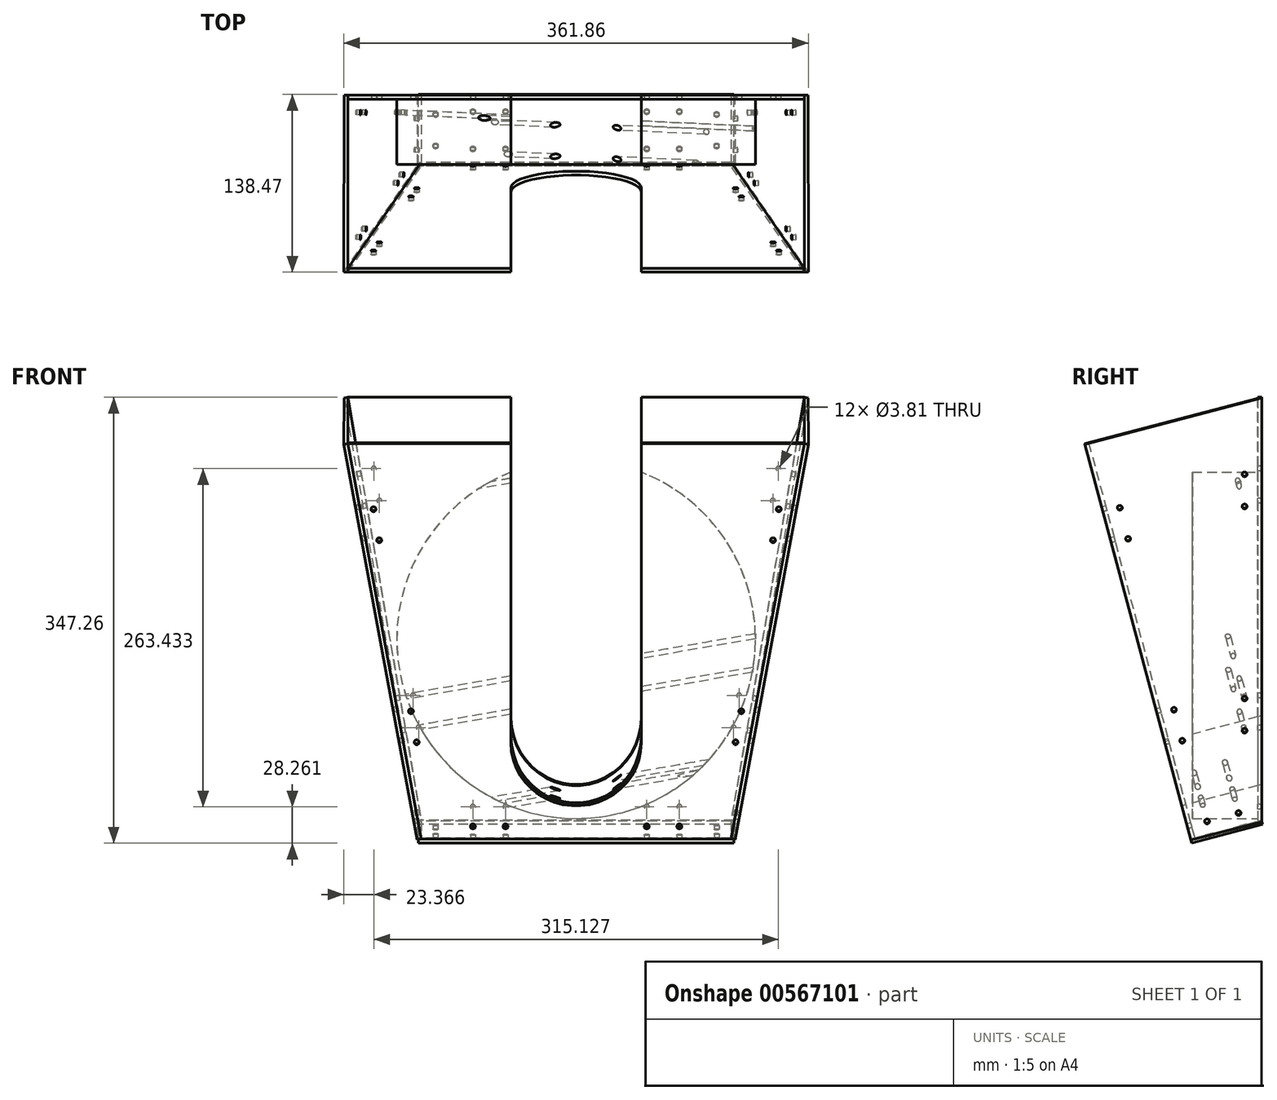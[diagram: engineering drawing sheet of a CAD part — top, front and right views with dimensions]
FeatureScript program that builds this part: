
annotation { "Feature Type Name" : "Feature", "Feature Type Description" : "" }
export const myFeature = defineFeature(function(context is Context, id is Id, definition is map)
    precondition{}
    {
        {
            var Q0;
            Q0=qCreatedBy(makeId("Right.planeOp"),FACE);
            var sketch = newSketch(context, id + "F0", { "sketchPlane" : qUnion([Q0])});
            skLineSegment(sketch, "E0.bottom", {"start": v(-164.52, 79.35) * mm, "end": v(-89.48, 66.12) * mm});
            skLineSegment(sketch, "E0.top", {"start": v(-67.49, 629.66) * mm, "end": v(7.56, 616.43) * mm});
            skLineSegment(sketch, "E0.left", {"start": v(-164.52, 79.35) * mm, "end": v(-67.49, 629.66) * mm});
            skLineSegment(sketch, "E0.right", {"start": v(-89.48, 66.12) * mm, "end": v(7.56, 616.43) * mm});
            skLineSegment(sketch, "E1.bottom", {"start": v(0, 38.1) * mm, "end": v(406.4, 38.1) * mm});
            skLineSegment(sketch, "E1.top", {"start": v(0, 546.1) * mm, "end": v(406.4, 546.1) * mm});
            skLineSegment(sketch, "E1.left", {"start": v(0, 38.1) * mm, "end": v(0, 546.1) * mm});
            skLineSegment(sketch, "E1.right", {"start": v(406.4, 38.1) * mm, "end": v(406.4, 546.1) * mm});
            skLineSegment(sketch, "E2.bottom", {"start": v(42.48, 128.48) * mm, "end": v(86.93, 128.48) * mm});
            skLineSegment(sketch, "E2.top", {"start": v(42.48, 84.03) * mm, "end": v(86.93, 84.03) * mm});
            skLineSegment(sketch, "E2.left", {"start": v(42.48, 128.48) * mm, "end": v(42.48, 84.03) * mm});
            skLineSegment(sketch, "E2.right", {"start": v(86.93, 128.48) * mm, "end": v(86.93, 84.03) * mm});
            skPoint(sketch, "E2.middle", {"position": v(64.7, 106.26) * mm});
            skSolve(sketch);
        }
        {
            var Q0;
            Q0=qCreatedBy(makeId("Front.planeOp"),FACE);
            var sketch = newSketch(context, id + "F1", { "sketchPlane" : qUnion([Q0])});
            skLineSegment(sketch, "E3.bottom", {"start": v(177.8, 596.9) * mm, "end": v(-177.8, 596.9) * mm});
            skLineSegment(sketch, "E3.top", {"start": v(120.65, 266.7) * mm, "end": v(-120.65, 266.7) * mm});
            skPoint(sketch, "E3.middle", {"position": v(0, 431.8) * mm});
            skLineSegment(sketch, "E4", {"start": v(-177.8, 596.9) * mm, "end": v(-120.65, 266.7) * mm});
            skLineSegment(sketch, "E5", {"start": v(0, 596.9) * mm, "end": v(0, 604.14) * mm, "construction": true});
            skPoint(sketch, "E5.endSnap0", {"position": v(0, 596.9) * mm});
            skLineSegment(sketch, "E6.MirrorCS", {"start": v(177.8, 596.9) * mm, "end": v(120.65, 266.7) * mm});
            skCircle(sketch, "E7", {"center": v(0, 408.44) * mm, "radius": 139.7 * mm, "construction": true});
            skCircle(sketch, "E8", {"center": v(0, 330.2) * mm, "radius": 17.46 * mm, "construction": true});
            skPoint(sketch, "E3.left.end.orphan", {"position": v(177.8, 266.7) * mm});
            skPoint(sketch, "E9.orphan", {"position": v(-177.8, 266.7) * mm});
            skSolve(sketch);
        }
        {
            var Q0;
            Q0=qSketchRegion(id+"F1",true);
            extrude(context, id + "F2", {"entities" : qUnion([Q0]), "oppositeDirection" : true, "depth" : 3.17 * mm});
        }
        {
            var Q0;
            Q0=makeQuery(id+"F1.imprint","IMPRINT",FACE,{"disambiguationData":[TD([[makeQuery(id+"F1.imprint","IMPRINT",EDGE,{"derivedFrom":sQuery(id+"F1.wireOp",EDGE,"E3.bottom")}),1.0]])]});
            var sketch = newSketch(context, id + "F3", { "sketchPlane" : qUnion([Q0])});
            skCircle(sketch, "E10.0", {"center": v(0, 408.44) * mm, "radius": 139.7 * mm});
            skSolve(sketch);
        }
        {
            var Q0;
            Q0=qSketchRegion(id+"F3",true);
            extrude(context, id + "F4", {"entities" : qUnion([Q0]), "depth" : 50.8 * mm});
        }
        {
            var Q0;
            Q0=makeQuery(id+"F4.opExtrude","CAP_FACE",FACE,{"disambiguationData":[OSD([sQuery(id+"F3.wireOp",EDGE,"E10.0")])],"isStart":false});
            var Q1;
            Q1=sQuery(id+"F1.wireOp",EDGE,"E3.top");
            cPlane(context, id + "F5", {"entities" : qUnion([Q0, Q1]), "cplaneType" : CPlaneType.LINE_ANGLE, "offset" : 25.4 * mm, "angle" : 345 * degree, "width" : 152.4 * mm, "height" : 152.4 * mm});
        }
        {
            var Q0;
            Q0=qCreatedBy(id+"F5.planeOp",FACE);
            cPlane(context, id + "F6", {"entities" : qUnion([Q0]), "cplaneType" : CPlaneType.OFFSET, "offset" : 53.97 * mm, "oppositeDirection" : true, "width" : 152.4 * mm, "height" : 152.4 * mm});
        }
        {
            var Q0;
            Q0=qCreatedBy(id+"F6.planeOp",FACE);
            var sketch = newSketch(context, id + "F7", { "sketchPlane" : qUnion([Q0])});
            skLineSegment(sketch, "E11.0", {"start": v(177.8, 576.56) * mm, "end": v(120.65, 257.61) * mm});
            skLineSegment(sketch, "E11.1", {"start": v(-177.8, 576.56) * mm, "end": v(177.8, 576.56) * mm});
            skLineSegment(sketch, "E11.2", {"start": v(-177.8, 576.56) * mm, "end": v(-120.65, 257.61) * mm});
            skLineSegment(sketch, "E11.3", {"start": v(-120.65, 257.61) * mm, "end": v(120.65, 257.61) * mm});
            skSolve(sketch);
        }
        {
            var Q0;
            Q0=makeQuery(id+"F7.imprint","IMPRINT",FACE,{"disambiguationData":[TD([[makeQuery(id+"F7.imprint","IMPRINT",EDGE,{"derivedFrom":sQuery(id+"F7.wireOp",EDGE,"E11.0")}),-1.0]])]});
            extrude(context, id + "F8", {"entities" : qUnion([Q0]), "depth" : 3.17 * mm});
        }
        {
            var Q0;
            Q0=makeQuery(id+"F8.opExtrude","SWEPT_FACE",FACE,{"disambiguationData":[OSD([sQuery(id+"F7.wireOp",EDGE,"E11.0")])]});
            var sketch = newSketch(context, id + "F9", { "sketchPlane" : qUnion([Q0])});
            skLineSegment(sketch, "E12.0", {"start": v(0.18, 618.48) * mm, "end": v(0.18, 283.37) * mm});
            skLineSegment(sketch, "E13.0", {"start": v(138.18, 582.92) * mm, "end": v(55.54, 269.6) * mm});
            skLineSegment(sketch, "E14", {"start": v(0.18, 283.37) * mm, "end": v(52.47, 270.41) * mm});
            skLineSegment(sketch, "E15", {"start": v(0.18, 618.48) * mm, "end": v(138.18, 582.92) * mm});
            skSolve(sketch);
        }
        {
            var Q0;
            {var subQ0=sQuery(id+"F9.wireOp",EDGE,"E12.0");Q0=makeQuery(id+"F9.imprint","IMPRINT",FACE,{"disambiguationData":[TD([[makeQuery(id+"F9.imprint","IMPRINT",EDGE,{"derivedFrom":subQ0}),1.0]])]});}
            var Q1;
            {var subQ0=sQuery(id+"F9.wireOp",EDGE,"E13.0");Q1=makeQuery(id+"F9.imprint","IMPRINT",FACE,{"disambiguationData":[TD([[makeQuery(id+"F9.imprint","IMPRINT",EDGE,{"derivedFrom":subQ0}),-1.0]])]});}
            extrude(context, id + "F10", {"entities" : qUnion([Q0, Q1]), "depth" : 3.17 * mm});
        }
        {
            var Q0;
            Q0=makeQuery(id+"F10.opExtrude","SWEPT_BODY",BODY,{"disambiguationData":[OSD([sQuery(id+"F7.wireOp",EDGE,"E11.0"),sQuery(id+"F9.wireOp",EDGE,"E12.0"),sQuery(id+"F9.wireOp",EDGE,"E14"),sQuery(id+"F9.wireOp",EDGE,"E15")])]});
            var Q1;
            Q1=qCreatedBy(makeId("Right.planeOp"),FACE);
            mirror(context, id + "F11", {"entities" : qUnion([Q0]), "mirrorPlane" : qUnion([Q1])});
        }
        {
            var Q0;
            Q0=makeQuery(id+"F8.opExtrude","SWEPT_FACE",FACE,{"disambiguationData":[OSD([sQuery(id+"F7.wireOp",EDGE,"E11.3")])]});
            var sketch = newSketch(context, id + "F12", { "sketchPlane" : qUnion([Q0])});
            skLineSegment(sketch, "E16.bottom", {"start": v(122.9, -15.05) * mm, "end": v(-122.9, -15.05) * mm});
            skLineSegment(sketch, "E16.top", {"start": v(122.9, -72.1) * mm, "end": v(-122.9, -72.1) * mm});
            skLineSegment(sketch, "E16.left", {"start": v(122.9, -15.05) * mm, "end": v(122.9, -72.1) * mm});
            skLineSegment(sketch, "E16.right", {"start": v(-122.9, -15.05) * mm, "end": v(-122.9, -72.1) * mm});
            skPoint(sketch, "E16.middle", {"position": v(0, -43.57) * mm});
            skSolve(sketch);
        }
        {
            var Q0;
            Q0=qSketchRegion(id+"F12",true);
            extrude(context, id + "F13", {"entities" : qUnion([Q0]), "depth" : 3.17 * mm});
        }
        {
            var Q0;
            Q0=makeQuery(id+"F8.opExtrude","CAP_FACE",FACE,{"disambiguationData":[OSD([sQuery(id+"F7.wireOp",EDGE,"E11.0"),sQuery(id+"F7.wireOp",EDGE,"E11.1"),sQuery(id+"F7.wireOp",EDGE,"E11.2"),sQuery(id+"F7.wireOp",EDGE,"E11.3")])],"isStart":true});
            var sketch = newSketch(context, id + "F14", { "sketchPlane" : qUnion([Q0])});
            skLineSegment(sketch, "E17", {"start": v(0, 439.09) * mm, "end": v(0, 333.36) * mm, "construction": true});
            skLineSegment(sketch, "E18.bottom", {"start": v(-170.23, 534.32) * mm, "end": v(-149.92, 537.96) * mm, "construction": true});
            skLineSegment(sketch, "E18.top", {"start": v(-161.27, 484.32) * mm, "end": v(-140.96, 487.96) * mm, "construction": true});
            skLineSegment(sketch, "E18.left", {"start": v(-170.23, 534.32) * mm, "end": v(-161.27, 484.32) * mm, "construction": true});
            skLineSegment(sketch, "E18.right", {"start": v(-149.92, 537.96) * mm, "end": v(-140.96, 487.96) * mm, "construction": true});
            skLineSegment(sketch, "E19.bottom", {"start": v(-93.12, 278.25) * mm, "end": v(-42.32, 278.25) * mm, "construction": true});
            skLineSegment(sketch, "E19.top", {"start": v(-93.12, 257.61) * mm, "end": v(-42.32, 257.61) * mm});
            skLineSegment(sketch, "E19.left", {"start": v(-93.12, 278.25) * mm, "end": v(-93.12, 257.61) * mm, "construction": true});
            skLineSegment(sketch, "E19.right", {"start": v(-42.32, 278.25) * mm, "end": v(-42.32, 257.61) * mm, "construction": true});
            skLineSegment(sketch, "E20", {"start": v(-160.07, 536.14) * mm, "end": v(-151.11, 486.14) * mm, "construction": true});
            skLineSegment(sketch, "E21", {"start": v(-93.12, 267.93) * mm, "end": v(-42.32, 267.93) * mm, "construction": true});
            skLineSegment(sketch, "E22", {"start": v(-145.44, 512.96) * mm, "end": v(-165.75, 509.32) * mm, "construction": true});
            skLineSegment(sketch, "E23", {"start": v(-67.72, 278.25) * mm, "end": v(-67.72, 257.61) * mm, "construction": true});
            skCircle(sketch, "E24", {"center": v(-157.83, 523.64) * mm, "radius": 1.9 * mm});
            skCircle(sketch, "E25.MirrorC", {"center": v(-153.35, 498.64) * mm, "radius": 1.9 * mm});
            skLineSegment(sketch, "E26.bottom", {"start": v(-141.04, 371.42) * mm, "end": v(-120.73, 375.06) * mm, "construction": true});
            skLineSegment(sketch, "E26.top", {"start": v(-132.08, 321.41) * mm, "end": v(-111.77, 325.05) * mm, "construction": true});
            skLineSegment(sketch, "E26.left", {"start": v(-141.04, 371.42) * mm, "end": v(-132.08, 321.41) * mm, "construction": true});
            skLineSegment(sketch, "E26.right", {"start": v(-120.73, 375.06) * mm, "end": v(-111.77, 325.05) * mm, "construction": true});
            skLineSegment(sketch, "E27", {"start": v(-130.88, 373.24) * mm, "end": v(-121.92, 323.23) * mm, "construction": true});
            skLineSegment(sketch, "E28", {"start": v(-116.25, 350.05) * mm, "end": v(-136.56, 346.41) * mm, "construction": true});
            skCircle(sketch, "E29", {"center": v(-128.64, 360.73) * mm, "radius": 1.9 * mm});
            skCircle(sketch, "E30.MirrorC", {"center": v(-124.16, 335.73) * mm, "radius": 1.9 * mm});
            skCircle(sketch, "E31", {"center": v(-80.42, 267.93) * mm, "radius": 1.9 * mm});
            skCircle(sketch, "E32.MirrorC", {"center": v(-55.02, 267.93) * mm, "radius": 1.9 * mm});
            skLineSegment(sketch, "E33.MirrorCS", {"start": v(132.08, 321.41) * mm, "end": v(111.77, 325.05) * mm, "construction": true});
            skCircle(sketch, "E34.MirrorC", {"center": v(128.64, 360.73) * mm, "radius": 1.9 * mm});
            skCircle(sketch, "E35.MirrorC", {"center": v(157.83, 523.64) * mm, "radius": 1.9 * mm});
            skLineSegment(sketch, "E36.MirrorCS", {"start": v(42.32, 278.25) * mm, "end": v(42.32, 257.61) * mm, "construction": true});
            skLineSegment(sketch, "E37.MirrorCS", {"start": v(93.12, 278.25) * mm, "end": v(93.12, 257.61) * mm, "construction": true});
            skLineSegment(sketch, "E38.MirrorCS", {"start": v(161.27, 484.32) * mm, "end": v(140.96, 487.96) * mm, "construction": true});
            skCircle(sketch, "E39.MirrorC", {"center": v(55.02, 267.93) * mm, "radius": 1.9 * mm});
            skLineSegment(sketch, "E40.MirrorCS", {"start": v(145.44, 512.96) * mm, "end": v(165.75, 509.32) * mm, "construction": true});
            skLineSegment(sketch, "E41.MirrorCS", {"start": v(170.23, 534.32) * mm, "end": v(149.92, 537.96) * mm, "construction": true});
            skLineSegment(sketch, "E42.MirrorCS", {"start": v(130.88, 373.24) * mm, "end": v(121.92, 323.23) * mm, "construction": true});
            skCircle(sketch, "E43.MirrorC", {"center": v(124.16, 335.73) * mm, "radius": 1.9 * mm});
            skLineSegment(sketch, "E44.MirrorCS", {"start": v(160.07, 536.14) * mm, "end": v(151.11, 486.14) * mm, "construction": true});
            skLineSegment(sketch, "E45.MirrorCS", {"start": v(141.04, 371.42) * mm, "end": v(120.73, 375.06) * mm, "construction": true});
            skCircle(sketch, "E46.MirrorC", {"center": v(153.35, 498.64) * mm, "radius": 1.9 * mm});
            skCircle(sketch, "E47.MirrorC", {"center": v(80.42, 267.93) * mm, "radius": 1.9 * mm});
            skLineSegment(sketch, "E48.MirrorCS", {"start": v(141.04, 371.42) * mm, "end": v(132.08, 321.41) * mm, "construction": true});
            skLineSegment(sketch, "E49.MirrorCS", {"start": v(93.12, 257.61) * mm, "end": v(42.32, 257.61) * mm});
            skLineSegment(sketch, "E50.MirrorCS", {"start": v(116.25, 350.05) * mm, "end": v(136.56, 346.41) * mm, "construction": true});
            skLineSegment(sketch, "E51.MirrorCS", {"start": v(170.23, 534.32) * mm, "end": v(161.27, 484.32) * mm, "construction": true});
            skLineSegment(sketch, "E52.MirrorCS", {"start": v(149.92, 537.96) * mm, "end": v(140.96, 487.96) * mm, "construction": true});
            skLineSegment(sketch, "E53.MirrorCS", {"start": v(120.73, 375.06) * mm, "end": v(111.77, 325.05) * mm, "construction": true});
            skLineSegment(sketch, "E54.MirrorCS", {"start": v(93.12, 267.93) * mm, "end": v(42.32, 267.93) * mm, "construction": true});
            skLineSegment(sketch, "E55.MirrorCS", {"start": v(67.72, 278.25) * mm, "end": v(67.72, 257.61) * mm, "construction": true});
            skLineSegment(sketch, "E56.MirrorCS", {"start": v(93.12, 278.25) * mm, "end": v(42.32, 278.25) * mm, "construction": true});
            skSolve(sketch);
        }
        {
            var Q0;
            Q0=qSketchRegion(id+"F14",true);
            var Q1;
            Q1=makeQuery(id+"F8.opExtrude","CAP_FACE",FACE,{"disambiguationData":[OSD([sQuery(id+"F7.wireOp",EDGE,"E11.0"),sQuery(id+"F7.wireOp",EDGE,"E11.1"),sQuery(id+"F7.wireOp",EDGE,"E11.2"),sQuery(id+"F7.wireOp",EDGE,"E11.3")])],"isStart":false});
            extrude(context, id + "F15", {"entities" : qUnion([Q0]), "operationType" : NewBodyOperationType.REMOVE, "endBound" : BoundingType.UP_TO_SURFACE, "oppositeDirection" : true, "depth" : 25.4 * mm, "endBoundEntityFace" : qUnion([Q1]), "offsetDistance" : 25.4 * mm});
        }
        {
            var Q0;
            Q0=makeQuery(id+"F10.opExtrude","CAP_FACE",FACE,{"disambiguationData":[OSD([sQuery(id+"F7.wireOp",EDGE,"E11.0"),sQuery(id+"F7.wireOp",EDGE,"E11.3"),sQuery(id+"F9.wireOp",EDGE,"E12.0"),sQuery(id+"F9.wireOp",EDGE,"E13.0"),sQuery(id+"F9.wireOp",EDGE,"E14"),sQuery(id+"F9.wireOp",EDGE,"E15")])],"isStart":false});
            var sketch = newSketch(context, id + "F16", { "sketchPlane" : qUnion([Q0])});
            skLineSegment(sketch, "E57.0", {"start": v(127.23, 541.42) * mm, "end": v(114.28, 492.3) * mm, "construction": true});
            skLineSegment(sketch, "E58.0", {"start": v(85.03, 381.4) * mm, "end": v(72.07, 332.28) * mm, "construction": true});
            skLineSegment(sketch, "E59.bottom", {"start": v(62, 387.47) * mm, "end": v(85.03, 381.4) * mm, "construction": true});
            skLineSegment(sketch, "E59.top", {"start": v(49.05, 338.35) * mm, "end": v(72.07, 332.28) * mm, "construction": true});
            skLineSegment(sketch, "E59.left", {"start": v(62, 387.47) * mm, "end": v(49.05, 338.35) * mm, "construction": true});
            skLineSegment(sketch, "E60", {"start": v(81.96, 382.2) * mm, "end": v(69, 333.09) * mm, "construction": true});
            skPoint(sketch, "E61", {"position": v(71.98, 384.84) * mm});
            skLineSegment(sketch, "E62", {"start": v(71.98, 384.84) * mm, "end": v(59.02, 335.72) * mm, "construction": true});
            skLineSegment(sketch, "E63", {"start": v(55.52, 362.9) * mm, "end": v(75.48, 357.65) * mm, "construction": true});
            skCircle(sketch, "E64", {"center": v(62.26, 348) * mm, "radius": 1.9 * mm});
            skCircle(sketch, "E65.MirrorC", {"center": v(68.74, 372.56) * mm, "radius": 1.9 * mm});
            skLineSegment(sketch, "E66.bottom", {"start": v(104.2, 547.5) * mm, "end": v(127.23, 541.42) * mm, "construction": true});
            skLineSegment(sketch, "E66.top", {"start": v(91.25, 498.37) * mm, "end": v(114.28, 492.3) * mm, "construction": true});
            skLineSegment(sketch, "E66.left", {"start": v(104.2, 547.5) * mm, "end": v(91.25, 498.37) * mm, "construction": true});
            skLineSegment(sketch, "E67", {"start": v(124.16, 542.23) * mm, "end": v(111.2, 493.11) * mm, "construction": true});
            skPoint(sketch, "E68", {"position": v(114.18, 544.86) * mm});
            skLineSegment(sketch, "E69", {"start": v(114.18, 544.86) * mm, "end": v(101.23, 495.74) * mm, "construction": true});
            skLineSegment(sketch, "E70", {"start": v(97.73, 522.93) * mm, "end": v(117.68, 517.67) * mm, "construction": true});
            skCircle(sketch, "E71", {"center": v(104.47, 508.02) * mm, "radius": 1.9 * mm});
            skCircle(sketch, "E72.MirrorC", {"center": v(110.95, 532.58) * mm, "radius": 1.9 * mm});
            skLineSegment(sketch, "E73.bottom", {"start": v(3.35, 570.93) * mm, "end": v(24, 570.93) * mm, "construction": true});
            skLineSegment(sketch, "E73.top", {"start": v(3.35, 520.13) * mm, "end": v(24, 520.13) * mm, "construction": true});
            skLineSegment(sketch, "E73.left", {"start": v(3.35, 570.93) * mm, "end": v(3.35, 520.13) * mm, "construction": true});
            skLineSegment(sketch, "E73.right", {"start": v(24, 570.93) * mm, "end": v(24, 520.13) * mm, "construction": true});
            skLineSegment(sketch, "E74.bottom", {"start": v(3.35, 570.93) * mm, "end": v(0.18, 570.93) * mm, "construction": true});
            skLineSegment(sketch, "E74.top", {"start": v(3.35, 520.13) * mm, "end": v(0.18, 520.13) * mm, "construction": true});
            skLineSegment(sketch, "E74.right", {"start": v(0.18, 570.93) * mm, "end": v(0.18, 520.13) * mm, "construction": true});
            skLineSegment(sketch, "E75", {"start": v(13.67, 570.93) * mm, "end": v(13.67, 520.13) * mm, "construction": true});
            skLineSegment(sketch, "E76", {"start": v(24, 545.53) * mm, "end": v(3.35, 545.53) * mm, "construction": true});
            skCircle(sketch, "E77", {"center": v(13.67, 558.23) * mm, "radius": 1.9 * mm});
            skCircle(sketch, "E78.MirrorC", {"center": v(13.67, 532.83) * mm, "radius": 1.9 * mm});
            skLineSegment(sketch, "E79.bottom", {"start": v(3.35, 393.68) * mm, "end": v(24, 393.68) * mm, "construction": true});
            skLineSegment(sketch, "E79.top", {"start": v(3.35, 342.88) * mm, "end": v(24, 342.88) * mm, "construction": true});
            skLineSegment(sketch, "E79.left", {"start": v(3.35, 393.68) * mm, "end": v(3.35, 342.88) * mm, "construction": true});
            skLineSegment(sketch, "E79.right", {"start": v(24, 393.68) * mm, "end": v(24, 342.88) * mm, "construction": true});
            skLineSegment(sketch, "E80.bottom", {"start": v(3.35, 393.68) * mm, "end": v(0.18, 393.68) * mm, "construction": true});
            skLineSegment(sketch, "E80.top", {"start": v(3.35, 342.88) * mm, "end": v(0.18, 342.88) * mm, "construction": true});
            skLineSegment(sketch, "E80.right", {"start": v(0.18, 393.68) * mm, "end": v(0.18, 342.88) * mm, "construction": true});
            skLineSegment(sketch, "E81", {"start": v(13.67, 393.68) * mm, "end": v(13.67, 342.88) * mm, "construction": true});
            skLineSegment(sketch, "E82", {"start": v(24, 368.28) * mm, "end": v(3.35, 368.28) * mm, "construction": true});
            skCircle(sketch, "E83", {"center": v(13.67, 380.98) * mm, "radius": 1.9 * mm});
            skCircle(sketch, "E84.MirrorC", {"center": v(13.67, 355.58) * mm, "radius": 1.9 * mm});
            skLineSegment(sketch, "E85.bottom", {"start": v(8.73, 303.76) * mm, "end": v(57.85, 290.8) * mm, "construction": true});
            skLineSegment(sketch, "E85.top", {"start": v(3.46, 283.8) * mm, "end": v(52.58, 270.85) * mm, "construction": true});
            skLineSegment(sketch, "E85.left", {"start": v(8.73, 303.76) * mm, "end": v(3.46, 283.8) * mm, "construction": true});
            skLineSegment(sketch, "E85.right", {"start": v(57.85, 290.8) * mm, "end": v(52.58, 270.85) * mm, "construction": true});
            skLineSegment(sketch, "E86.top", {"start": v(2.65, 280.73) * mm, "end": v(51.77, 267.78) * mm, "construction": true});
            skLineSegment(sketch, "E86.left", {"start": v(3.46, 283.8) * mm, "end": v(2.65, 280.73) * mm, "construction": true});
            skLineSegment(sketch, "E86.right", {"start": v(52.58, 270.85) * mm, "end": v(51.77, 267.78) * mm, "construction": true});
            skLineSegment(sketch, "E87", {"start": v(6.1, 293.78) * mm, "end": v(55.22, 280.82) * mm, "construction": true});
            skLineSegment(sketch, "E88", {"start": v(33.29, 297.28) * mm, "end": v(28.02, 277.32) * mm, "construction": true});
            skCircle(sketch, "E89", {"center": v(18.38, 290.54) * mm, "radius": 1.9 * mm});
            skCircle(sketch, "E90.MirrorC", {"center": v(42.94, 284.06) * mm, "radius": 1.9 * mm});
            skSolve(sketch);
        }
        {
            var Q0;
            Q0=qSketchRegion(id+"F16",true);
            extrude(context, id + "F17", {"entities" : qUnion([Q0]), "operationType" : NewBodyOperationType.REMOVE, "endBound" : BoundingType.THROUGH_ALL, "oppositeDirection" : true, "depth" : 25.4 * mm, "offsetDistance" : 25.4 * mm});
        }
        {
            var Q0;
            Q0=makeQuery(id+"F11.opPattern","COPY",BODY,{"derivedFrom":makeQuery(id+"F10.opExtrude","SWEPT_BODY",BODY,{"disambiguationData":[OSD([sQuery(id+"F7.wireOp",EDGE,"E11.0"),sQuery(id+"F7.wireOp",EDGE,"E11.3"),sQuery(id+"F9.wireOp",EDGE,"E12.0"),sQuery(id+"F9.wireOp",EDGE,"E13.0"),sQuery(id+"F9.wireOp",EDGE,"E14"),sQuery(id+"F9.wireOp",EDGE,"E15")])]}),"instanceName":"1"});
            deleteBodies(context, id + "F18", {"entities" : qUnion([Q0])});
        }
        {
            var Q0;
            Q0=makeQuery(id+"F10.opExtrude","SWEPT_BODY",BODY,{"disambiguationData":[OSD([sQuery(id+"F7.wireOp",EDGE,"E11.0"),sQuery(id+"F7.wireOp",EDGE,"E11.3"),sQuery(id+"F9.wireOp",EDGE,"E12.0"),sQuery(id+"F9.wireOp",EDGE,"E13.0"),sQuery(id+"F9.wireOp",EDGE,"E14"),sQuery(id+"F9.wireOp",EDGE,"E15")])]});
            var Q1;
            Q1=qCreatedBy(makeId("Right.planeOp"),FACE);
            mirror(context, id + "F19", {"entities" : qUnion([Q0]), "mirrorPlane" : qUnion([Q1])});
        }
        {
            var Q0;
            Q0=makeQuery(id+"F1.imprint","IMPRINT",FACE,{"disambiguationData":[TD([[makeQuery(id+"F1.imprint","IMPRINT",EDGE,{"derivedFrom":sQuery(id+"F1.wireOp",EDGE,"E3.bottom")}),1.0]])]});
            var sketch = newSketch(context, id + "F20", { "sketchPlane" : qUnion([Q0])});
            skLineSegment(sketch, "E91.0", {"start": v(-172.82, 549.5) * mm, "end": v(-164.15, 499.45) * mm, "construction": true});
            skLineSegment(sketch, "E92.bottom", {"start": v(-169.9, 552.1) * mm, "end": v(-173.03, 551.57) * mm, "construction": true});
            skLineSegment(sketch, "E92.top", {"start": v(-161.23, 502.05) * mm, "end": v(-164.36, 501.51) * mm, "construction": true});
            skLineSegment(sketch, "E92.left", {"start": v(-169.9, 552.1) * mm, "end": v(-161.23, 502.05) * mm, "construction": true});
            skLineSegment(sketch, "E92.right", {"start": v(-173.03, 551.57) * mm, "end": v(-164.36, 501.51) * mm, "construction": true});
            skLineSegment(sketch, "E93.bottom", {"start": v(-149.56, 555.63) * mm, "end": v(-169.9, 552.1) * mm, "construction": true});
            skLineSegment(sketch, "E93.top", {"start": v(-140.9, 505.57) * mm, "end": v(-161.23, 502.05) * mm, "construction": true});
            skLineSegment(sketch, "E93.left", {"start": v(-149.56, 555.63) * mm, "end": v(-140.9, 505.57) * mm, "construction": true});
            skLineSegment(sketch, "E94", {"start": v(-159.73, 553.87) * mm, "end": v(-151.07, 503.81) * mm, "construction": true});
            skLineSegment(sketch, "E95", {"start": v(-145.23, 530.6) * mm, "end": v(-165.57, 527.08) * mm, "construction": true});
            skCircle(sketch, "E96", {"center": v(-157.56, 541.35) * mm, "radius": 1.9 * mm});
            skCircle(sketch, "E97.MirrorC", {"center": v(-153.23, 516.33) * mm, "radius": 1.9 * mm});
            skLineSegment(sketch, "E98", {"start": v(0, 542.09) * mm, "end": v(0, 433.89) * mm, "construction": true});
            skLineSegment(sketch, "E99.0", {"start": v(-137.98, 349.1) * mm, "end": v(-129.32, 299.04) * mm, "construction": true});
            skLineSegment(sketch, "E100.bottom", {"start": v(-139.32, 375.42) * mm, "end": v(-142.45, 374.88) * mm, "construction": true});
            skLineSegment(sketch, "E100.top", {"start": v(-130.65, 325.37) * mm, "end": v(-133.78, 324.83) * mm, "construction": true});
            skLineSegment(sketch, "E100.left", {"start": v(-139.32, 375.42) * mm, "end": v(-130.65, 325.37) * mm, "construction": true});
            skLineSegment(sketch, "E100.right", {"start": v(-142.45, 374.88) * mm, "end": v(-133.78, 324.83) * mm, "construction": true});
            skLineSegment(sketch, "E101.bottom", {"start": v(-118.98, 378.94) * mm, "end": v(-139.32, 375.42) * mm, "construction": true});
            skLineSegment(sketch, "E101.top", {"start": v(-110.32, 328.89) * mm, "end": v(-130.65, 325.37) * mm, "construction": true});
            skLineSegment(sketch, "E101.left", {"start": v(-118.98, 378.94) * mm, "end": v(-110.32, 328.89) * mm, "construction": true});
            skLineSegment(sketch, "E102", {"start": v(-129.15, 377.18) * mm, "end": v(-120.49, 327.13) * mm, "construction": true});
            skLineSegment(sketch, "E103", {"start": v(-114.65, 353.92) * mm, "end": v(-134.99, 350.4) * mm, "construction": true});
            skCircle(sketch, "E104", {"center": v(-126.98, 364.67) * mm, "radius": 1.9 * mm});
            skCircle(sketch, "E105.MirrorC", {"center": v(-122.65, 339.64) * mm, "radius": 1.9 * mm});
            skLineSegment(sketch, "E106.bottom", {"start": v(-42.32, 288.24) * mm, "end": v(-93.12, 288.24) * mm, "construction": true});
            skLineSegment(sketch, "E106.top", {"start": v(-42.32, 267.6) * mm, "end": v(-93.12, 267.6) * mm, "construction": true});
            skLineSegment(sketch, "E106.left", {"start": v(-42.32, 288.24) * mm, "end": v(-42.32, 267.6) * mm, "construction": true});
            skLineSegment(sketch, "E106.right", {"start": v(-93.12, 288.24) * mm, "end": v(-93.12, 267.6) * mm, "construction": true});
            skLineSegment(sketch, "E107.top", {"start": v(-42.32, 264.43) * mm, "end": v(-93.12, 264.43) * mm, "construction": true});
            skLineSegment(sketch, "E107.left", {"start": v(-42.32, 267.6) * mm, "end": v(-42.32, 264.43) * mm, "construction": true});
            skLineSegment(sketch, "E107.right", {"start": v(-93.12, 267.6) * mm, "end": v(-93.12, 264.43) * mm, "construction": true});
            skLineSegment(sketch, "E108", {"start": v(-42.32, 277.92) * mm, "end": v(-93.12, 277.92) * mm, "construction": true});
            skLineSegment(sketch, "E109", {"start": v(-67.72, 288.24) * mm, "end": v(-67.72, 267.6) * mm, "construction": true});
            skCircle(sketch, "E110", {"center": v(-55.02, 277.92) * mm, "radius": 1.9 * mm});
            skCircle(sketch, "E111.MirrorC", {"center": v(-80.42, 277.92) * mm, "radius": 1.9 * mm});
            skLineSegment(sketch, "E112.MirrorCS", {"start": v(161.23, 502.05) * mm, "end": v(164.36, 501.51) * mm, "construction": true});
            skLineSegment(sketch, "E113.MirrorCS", {"start": v(169.9, 552.1) * mm, "end": v(173.03, 551.57) * mm, "construction": true});
            skLineSegment(sketch, "E114.MirrorCS", {"start": v(139.32, 375.42) * mm, "end": v(142.45, 374.88) * mm, "construction": true});
            skLineSegment(sketch, "E115.MirrorCS", {"start": v(130.65, 325.37) * mm, "end": v(133.78, 324.83) * mm, "construction": true});
            skLineSegment(sketch, "E116.MirrorCS", {"start": v(42.32, 267.6) * mm, "end": v(42.32, 264.43) * mm, "construction": true});
            skLineSegment(sketch, "E117.MirrorCS", {"start": v(93.12, 267.6) * mm, "end": v(93.12, 264.43) * mm, "construction": true});
            skLineSegment(sketch, "E118.MirrorCS", {"start": v(139.32, 375.42) * mm, "end": v(130.65, 325.37) * mm, "construction": true});
            skCircle(sketch, "E119.MirrorC", {"center": v(126.98, 364.67) * mm, "radius": 1.9 * mm});
            skLineSegment(sketch, "E120.MirrorCS", {"start": v(169.9, 552.1) * mm, "end": v(161.23, 502.05) * mm, "construction": true});
            skLineSegment(sketch, "E121.MirrorCS", {"start": v(172.82, 549.5) * mm, "end": v(164.15, 499.45) * mm, "construction": true});
            skLineSegment(sketch, "E122.MirrorCS", {"start": v(142.45, 374.88) * mm, "end": v(133.78, 324.83) * mm, "construction": true});
            skLineSegment(sketch, "E123.MirrorCS", {"start": v(173.03, 551.57) * mm, "end": v(164.36, 501.51) * mm, "construction": true});
            skLineSegment(sketch, "E124.MirrorCS", {"start": v(42.32, 264.43) * mm, "end": v(93.12, 264.43) * mm, "construction": true});
            skLineSegment(sketch, "E125.MirrorCS", {"start": v(129.15, 377.18) * mm, "end": v(120.49, 327.13) * mm, "construction": true});
            skLineSegment(sketch, "E126.MirrorCS", {"start": v(42.32, 288.24) * mm, "end": v(42.32, 267.6) * mm, "construction": true});
            skCircle(sketch, "E127.MirrorC", {"center": v(153.23, 516.33) * mm, "radius": 1.9 * mm});
            skLineSegment(sketch, "E128.MirrorCS", {"start": v(140.9, 505.57) * mm, "end": v(161.23, 502.05) * mm, "construction": true});
            skLineSegment(sketch, "E129.MirrorCS", {"start": v(149.56, 555.63) * mm, "end": v(169.9, 552.1) * mm, "construction": true});
            skLineSegment(sketch, "E130.MirrorCS", {"start": v(145.23, 530.6) * mm, "end": v(165.57, 527.08) * mm, "construction": true});
            skLineSegment(sketch, "E131.MirrorCS", {"start": v(118.98, 378.94) * mm, "end": v(110.32, 328.89) * mm, "construction": true});
            skLineSegment(sketch, "E132.MirrorCS", {"start": v(118.98, 378.94) * mm, "end": v(139.32, 375.42) * mm, "construction": true});
            skCircle(sketch, "E133.MirrorC", {"center": v(157.56, 541.35) * mm, "radius": 1.9 * mm});
            skLineSegment(sketch, "E134.MirrorCS", {"start": v(93.12, 288.24) * mm, "end": v(93.12, 267.6) * mm, "construction": true});
            skLineSegment(sketch, "E135.MirrorCS", {"start": v(159.73, 553.87) * mm, "end": v(151.07, 503.81) * mm, "construction": true});
            skLineSegment(sketch, "E136.MirrorCS", {"start": v(42.32, 267.6) * mm, "end": v(93.12, 267.6) * mm, "construction": true});
            skCircle(sketch, "E137.MirrorC", {"center": v(122.65, 339.64) * mm, "radius": 1.9 * mm});
            skLineSegment(sketch, "E138.MirrorCS", {"start": v(114.65, 353.92) * mm, "end": v(134.99, 350.4) * mm, "construction": true});
            skLineSegment(sketch, "E139.MirrorCS", {"start": v(110.32, 328.89) * mm, "end": v(130.65, 325.37) * mm, "construction": true});
            skLineSegment(sketch, "E140.MirrorCS", {"start": v(137.98, 349.1) * mm, "end": v(129.32, 299.04) * mm, "construction": true});
            skLineSegment(sketch, "E141.MirrorCS", {"start": v(149.56, 555.63) * mm, "end": v(140.9, 505.57) * mm, "construction": true});
            skLineSegment(sketch, "E142.MirrorCS", {"start": v(42.32, 277.92) * mm, "end": v(93.12, 277.92) * mm, "construction": true});
            skCircle(sketch, "E143.MirrorC", {"center": v(55.02, 277.92) * mm, "radius": 1.9 * mm});
            skLineSegment(sketch, "E144.MirrorCS", {"start": v(42.32, 288.24) * mm, "end": v(93.12, 288.24) * mm, "construction": true});
            skLineSegment(sketch, "E145.MirrorCS", {"start": v(67.72, 288.24) * mm, "end": v(67.72, 267.6) * mm, "construction": true});
            skCircle(sketch, "E146.MirrorC", {"center": v(80.42, 277.92) * mm, "radius": 1.9 * mm});
            skSolve(sketch);
        }
        {
            var Q0;
            Q0=qSketchRegion(id+"F20",true);
            var Q1;
            Q1=sQuery(id+"F20.wireOp",EDGE,"E96");
            var Q2;
            Q2=sQuery(id+"F20.wireOp",EDGE,"E97.MirrorC");
            var Q3;
            Q3=sQuery(id+"F20.wireOp",EDGE,"E127.MirrorC");
            var Q4;
            Q4=sQuery(id+"F20.wireOp",EDGE,"E133.MirrorC");
            var Q5;
            Q5=sQuery(id+"F20.wireOp",EDGE,"E119.MirrorC");
            var Q6;
            Q6=sQuery(id+"F20.wireOp",EDGE,"E137.MirrorC");
            var Q7;
            Q7=sQuery(id+"F20.wireOp",EDGE,"E146.MirrorC");
            var Q8;
            Q8=sQuery(id+"F20.wireOp",EDGE,"E143.MirrorC");
            var Q9;
            Q9=sQuery(id+"F20.wireOp",EDGE,"E110");
            var Q10;
            Q10=sQuery(id+"F20.wireOp",EDGE,"E111.MirrorC");
            var Q11;
            Q11=sQuery(id+"F20.wireOp",EDGE,"E104");
            var Q12;
            Q12=sQuery(id+"F20.wireOp",EDGE,"E105.MirrorC");
            var Q13;
            Q13=makeQuery(id+"F2.opExtrude","CAP_FACE",FACE,{"disambiguationData":[OSD([sQuery(id+"F1.wireOp",EDGE,"E3.bottom"),sQuery(id+"F1.wireOp",EDGE,"E3.top"),sQuery(id+"F1.wireOp",EDGE,"E4"),sQuery(id+"F1.wireOp",EDGE,"E6.MirrorCS")])],"isStart":false});
            extrude(context, id + "F21", {"entities" : qUnion([Q0]), "operationType" : NewBodyOperationType.REMOVE, "surfaceEntities" : qUnion([Q1, Q2, Q3, Q4, Q5, Q6, Q7, Q8, Q9, Q10, Q11, Q12]), "endBound" : BoundingType.UP_TO_SURFACE, "oppositeDirection" : true, "depth" : 25.4 * mm, "endBoundEntityFace" : qUnion([Q13]), "offsetDistance" : 25.4 * mm});
        }
        {
            var Q0;
            Q0=makeQuery(id+"F13.opExtrude","CAP_FACE",FACE,{"disambiguationData":[OSD([sQuery(id+"F12.wireOp",EDGE,"E16.bottom"),sQuery(id+"F12.wireOp",EDGE,"E16.top"),sQuery(id+"F12.wireOp",EDGE,"E16.left"),sQuery(id+"F12.wireOp",EDGE,"E16.right")])],"isStart":false});
            var sketch = newSketch(context, id + "F22", { "sketchPlane" : qUnion([Q0])});
            skLineSegment(sketch, "E147", {"start": v(0, -15.05) * mm, "end": v(0, -38.18) * mm, "construction": true});
            skLineSegment(sketch, "E148.bottom", {"start": v(-93.12, -18.23) * mm, "end": v(-42.32, -18.23) * mm, "construction": true});
            skLineSegment(sketch, "E148.top", {"start": v(-93.12, -38.86) * mm, "end": v(-42.32, -38.86) * mm, "construction": true});
            skLineSegment(sketch, "E148.left", {"start": v(-93.12, -18.23) * mm, "end": v(-93.12, -38.86) * mm, "construction": true});
            skLineSegment(sketch, "E148.right", {"start": v(-42.32, -18.23) * mm, "end": v(-42.32, -38.86) * mm, "construction": true});
            skLineSegment(sketch, "E149.top", {"start": v(-93.12, -15.05) * mm, "end": v(-42.32, -15.05) * mm, "construction": true});
            skLineSegment(sketch, "E149.left", {"start": v(-93.12, -18.23) * mm, "end": v(-93.12, -15.05) * mm, "construction": true});
            skLineSegment(sketch, "E149.right", {"start": v(-42.32, -18.23) * mm, "end": v(-42.32, -15.05) * mm, "construction": true});
            skLineSegment(sketch, "E150", {"start": v(-93.12, -28.55) * mm, "end": v(-42.32, -28.55) * mm, "construction": true});
            skLineSegment(sketch, "E151", {"start": v(-67.72, -38.86) * mm, "end": v(-67.72, -18.23) * mm, "construction": true});
            skCircle(sketch, "E152", {"center": v(-80.42, -28.55) * mm, "radius": 1.9 * mm});
            skCircle(sketch, "E153.MirrorC", {"center": v(-55.02, -28.55) * mm, "radius": 1.9 * mm});
            skLineSegment(sketch, "E154.bottom", {"start": v(-93.12, -48.28) * mm, "end": v(-42.32, -48.28) * mm, "construction": true});
            skLineSegment(sketch, "E154.top", {"start": v(-93.12, -68.92) * mm, "end": v(-42.32, -68.92) * mm, "construction": true});
            skLineSegment(sketch, "E154.left", {"start": v(-93.12, -48.28) * mm, "end": v(-93.12, -68.92) * mm, "construction": true});
            skLineSegment(sketch, "E154.right", {"start": v(-42.32, -48.28) * mm, "end": v(-42.32, -68.92) * mm, "construction": true});
            skLineSegment(sketch, "E155.top", {"start": v(-93.12, -72.1) * mm, "end": v(-42.32, -72.1) * mm, "construction": true});
            skLineSegment(sketch, "E155.left", {"start": v(-93.12, -68.92) * mm, "end": v(-93.12, -72.1) * mm, "construction": true});
            skLineSegment(sketch, "E155.right", {"start": v(-42.32, -68.92) * mm, "end": v(-42.32, -72.1) * mm, "construction": true});
            skLineSegment(sketch, "E156", {"start": v(-67.72, -48.28) * mm, "end": v(-67.72, -68.92) * mm, "construction": true});
            skLineSegment(sketch, "E157", {"start": v(-93.12, -58.6) * mm, "end": v(-42.32, -58.6) * mm, "construction": true});
            skCircle(sketch, "E158", {"center": v(-80.42, -58.6) * mm, "radius": 1.9 * mm});
            skCircle(sketch, "E159.MirrorC", {"center": v(-55.02, -58.6) * mm, "radius": 1.9 * mm});
            skLineSegment(sketch, "E160.bottom", {"start": v(-119.72, -18.23) * mm, "end": v(-99.09, -18.23) * mm, "construction": true});
            skLineSegment(sketch, "E160.top", {"start": v(-119.72, -69.03) * mm, "end": v(-99.09, -69.03) * mm, "construction": true});
            skLineSegment(sketch, "E160.left", {"start": v(-119.72, -18.23) * mm, "end": v(-119.72, -69.03) * mm, "construction": true});
            skLineSegment(sketch, "E160.right", {"start": v(-99.09, -18.23) * mm, "end": v(-99.09, -69.03) * mm, "construction": true});
            skLineSegment(sketch, "E161.bottom", {"start": v(-119.72, -18.23) * mm, "end": v(-122.9, -18.23) * mm, "construction": true});
            skLineSegment(sketch, "E161.top", {"start": v(-119.72, -69.03) * mm, "end": v(-122.9, -69.03) * mm, "construction": true});
            skLineSegment(sketch, "E161.right", {"start": v(-122.9, -18.23) * mm, "end": v(-122.9, -69.03) * mm, "construction": true});
            skLineSegment(sketch, "E162", {"start": v(-99.09, -43.63) * mm, "end": v(-119.72, -43.63) * mm, "construction": true});
            skLineSegment(sketch, "E163", {"start": v(-109.4, -18.23) * mm, "end": v(-109.4, -69.03) * mm, "construction": true});
            skCircle(sketch, "E164", {"center": v(-109.4, -30.93) * mm, "radius": 1.9 * mm});
            skCircle(sketch, "E165.MirrorC", {"center": v(-109.4, -56.33) * mm, "radius": 1.9 * mm});
            skLineSegment(sketch, "E166.MirrorCS", {"start": v(93.12, -18.23) * mm, "end": v(93.12, -15.05) * mm, "construction": true});
            skLineSegment(sketch, "E167.MirrorCS", {"start": v(42.32, -18.23) * mm, "end": v(42.32, -15.05) * mm, "construction": true});
            skLineSegment(sketch, "E168.MirrorCS", {"start": v(119.72, -18.23) * mm, "end": v(122.9, -18.23) * mm, "construction": true});
            skLineSegment(sketch, "E169.MirrorCS", {"start": v(119.72, -69.03) * mm, "end": v(122.9, -69.03) * mm, "construction": true});
            skLineSegment(sketch, "E170.MirrorCS", {"start": v(42.32, -68.92) * mm, "end": v(42.32, -72.1) * mm, "construction": true});
            skLineSegment(sketch, "E171.MirrorCS", {"start": v(93.12, -68.92) * mm, "end": v(93.12, -72.1) * mm, "construction": true});
            skLineSegment(sketch, "E172.MirrorCS", {"start": v(93.12, -18.23) * mm, "end": v(42.32, -18.23) * mm, "construction": true});
            skLineSegment(sketch, "E173.MirrorCS", {"start": v(119.72, -18.23) * mm, "end": v(119.72, -69.03) * mm, "construction": true});
            skLineSegment(sketch, "E174.MirrorCS", {"start": v(93.12, -68.92) * mm, "end": v(42.32, -68.92) * mm, "construction": true});
            skCircle(sketch, "E175.MirrorC", {"center": v(109.4, -30.93) * mm, "radius": 1.9 * mm});
            skLineSegment(sketch, "E176.MirrorCS", {"start": v(93.12, -38.86) * mm, "end": v(42.32, -38.86) * mm, "construction": true});
            skCircle(sketch, "E177.MirrorC", {"center": v(80.42, -58.6) * mm, "radius": 1.9 * mm});
            skLineSegment(sketch, "E178.MirrorCS", {"start": v(42.32, -48.28) * mm, "end": v(42.32, -68.92) * mm, "construction": true});
            skLineSegment(sketch, "E179.MirrorCS", {"start": v(93.12, -48.28) * mm, "end": v(93.12, -68.92) * mm, "construction": true});
            skLineSegment(sketch, "E180.MirrorCS", {"start": v(122.9, -18.23) * mm, "end": v(122.9, -69.03) * mm, "construction": true});
            skLineSegment(sketch, "E181.MirrorCS", {"start": v(119.72, -18.23) * mm, "end": v(99.09, -18.23) * mm, "construction": true});
            skLineSegment(sketch, "E182.MirrorCS", {"start": v(67.72, -48.28) * mm, "end": v(67.72, -68.92) * mm, "construction": true});
            skLineSegment(sketch, "E183.MirrorCS", {"start": v(93.12, -18.23) * mm, "end": v(93.12, -38.86) * mm, "construction": true});
            skLineSegment(sketch, "E184.MirrorCS", {"start": v(93.12, -15.05) * mm, "end": v(42.32, -15.05) * mm, "construction": true});
            skLineSegment(sketch, "E185.MirrorCS", {"start": v(42.32, -18.23) * mm, "end": v(42.32, -38.86) * mm, "construction": true});
            skCircle(sketch, "E186.MirrorC", {"center": v(55.02, -58.6) * mm, "radius": 1.9 * mm});
            skLineSegment(sketch, "E187.MirrorCS", {"start": v(119.72, -69.03) * mm, "end": v(99.09, -69.03) * mm, "construction": true});
            skLineSegment(sketch, "E188.MirrorCS", {"start": v(99.09, -43.63) * mm, "end": v(119.72, -43.63) * mm, "construction": true});
            skLineSegment(sketch, "E189.MirrorCS", {"start": v(93.12, -48.28) * mm, "end": v(42.32, -48.28) * mm, "construction": true});
            skLineSegment(sketch, "E190.MirrorCS", {"start": v(99.09, -18.23) * mm, "end": v(99.09, -69.03) * mm, "construction": true});
            skCircle(sketch, "E191.MirrorC", {"center": v(55.02, -28.55) * mm, "radius": 1.9 * mm});
            skLineSegment(sketch, "E192.MirrorCS", {"start": v(93.12, -58.6) * mm, "end": v(42.32, -58.6) * mm, "construction": true});
            skCircle(sketch, "E193.MirrorC", {"center": v(109.4, -56.33) * mm, "radius": 1.9 * mm});
            skLineSegment(sketch, "E194.MirrorCS", {"start": v(93.12, -72.1) * mm, "end": v(42.32, -72.1) * mm, "construction": true});
            skLineSegment(sketch, "E195.MirrorCS", {"start": v(67.72, -38.86) * mm, "end": v(67.72, -18.23) * mm, "construction": true});
            skCircle(sketch, "E196.MirrorC", {"center": v(80.42, -28.55) * mm, "radius": 1.9 * mm});
            skLineSegment(sketch, "E197.MirrorCS", {"start": v(93.12, -28.55) * mm, "end": v(42.32, -28.55) * mm, "construction": true});
            skLineSegment(sketch, "E198.MirrorCS", {"start": v(109.4, -18.23) * mm, "end": v(109.4, -69.03) * mm, "construction": true});
            skSolve(sketch);
        }
        {
            var Q0;
            Q0=qSketchRegion(id+"F22",true);
            var Q1;
            Q1=makeQuery(id+"F13.opExtrude","CAP_FACE",FACE,{"disambiguationData":[OSD([sQuery(id+"F12.wireOp",EDGE,"E16.bottom"),sQuery(id+"F12.wireOp",EDGE,"E16.top"),sQuery(id+"F12.wireOp",EDGE,"E16.left"),sQuery(id+"F12.wireOp",EDGE,"E16.right")])],"isStart":true});
            extrude(context, id + "F23", {"entities" : qUnion([Q0]), "operationType" : NewBodyOperationType.REMOVE, "endBound" : BoundingType.UP_TO_SURFACE, "oppositeDirection" : true, "depth" : 25.4 * mm, "endBoundEntityFace" : qUnion([Q1]), "offsetDistance" : 25.4 * mm});
        }
        {
            var Q0;
            Q0=makeQuery(id+"F8.opExtrude","CAP_FACE",FACE,{"disambiguationData":[OSD([sQuery(id+"F7.wireOp",EDGE,"E11.0"),sQuery(id+"F7.wireOp",EDGE,"E11.1"),sQuery(id+"F7.wireOp",EDGE,"E11.2"),sQuery(id+"F7.wireOp",EDGE,"E11.3")])],"isStart":true});
            var sketch = newSketch(context, id + "F24", { "sketchPlane" : qUnion([Q0])});
            skLineSegment(sketch, "E199.top", {"start": v(50.8, 576.56) * mm, "end": v(-50.8, 576.56) * mm});
            skLineSegment(sketch, "E199.left", {"start": v(50.8, 334.36) * mm, "end": v(50.8, 576.56) * mm});
            skLineSegment(sketch, "E199.right", {"start": v(-50.8, 334.36) * mm, "end": v(-50.8, 576.56) * mm});
            skPoint(sketch, "E199.middle", {"position": v(0, 430.51) * mm});
            skLineSegment(sketch, "E200.0", {"start": v(177.8, 576.56) * mm, "end": v(-177.8, 576.56) * mm, "construction": true});
            skArc(sketch, "E201", {"start": v(-50.8, 336.18) * mm, "mid": v(0, 284.46) * mm, "end": v(50.8, 336.18) * mm});
            skPoint(sketch, "E202.orphan", {"position": v(-50.8, 284.46) * mm});
            skPoint(sketch, "E203.orphan", {"position": v(50.8, 284.46) * mm});
            skSolve(sketch);
        }
        {
            var Q0;
            Q0=qSketchRegion(id+"F24",true);
            var Q1;
            Q1=makeQuery(id+"F8.opExtrude","CAP_FACE",FACE,{"disambiguationData":[OSD([sQuery(id+"F7.wireOp",EDGE,"E11.0"),sQuery(id+"F7.wireOp",EDGE,"E11.1"),sQuery(id+"F7.wireOp",EDGE,"E11.2"),sQuery(id+"F7.wireOp",EDGE,"E11.3")])],"isStart":false});
            extrude(context, id + "F25", {"entities" : qUnion([Q0]), "operationType" : NewBodyOperationType.REMOVE, "endBound" : BoundingType.THROUGH_ALL, "oppositeDirection" : true, "depth" : 25.4 * mm, "endBoundEntityFace" : qUnion([Q1]), "offsetDistance" : 25.4 * mm});
        }
    });
